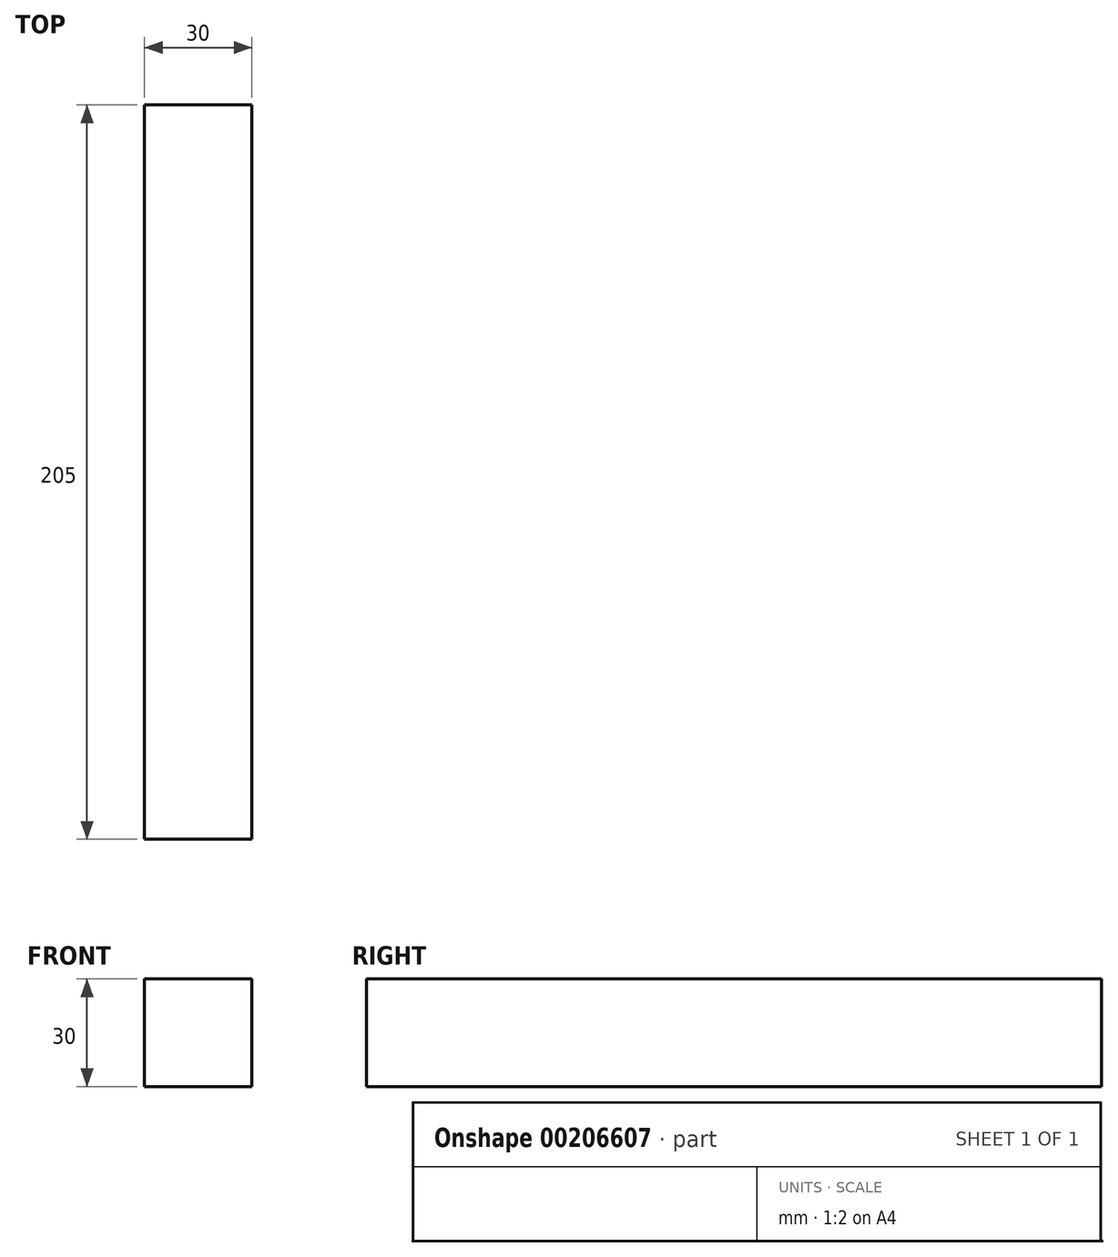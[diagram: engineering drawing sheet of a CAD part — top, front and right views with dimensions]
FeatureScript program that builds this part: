
annotation { "Feature Type Name" : "Feature", "Feature Type Description" : "" }
export const myFeature = defineFeature(function(context is Context, id is Id, definition is map)
    precondition{}
    {
        {
            var Q0;
            Q0=qCreatedBy(makeId("Front.planeOp"),FACE);
            var sketch = newSketch(context, id + "F0", { "sketchPlane" : qUnion([Q0])});
            skLineSegment(sketch, "E0.bottom", {"start": v(0, 0) * mm, "end": v(30, 0) * mm});
            skLineSegment(sketch, "E0.top", {"start": v(0, 30) * mm, "end": v(30, 30) * mm});
            skLineSegment(sketch, "E0.left", {"start": v(0, 0) * mm, "end": v(0, 30) * mm});
            skLineSegment(sketch, "E0.right", {"start": v(30, 0) * mm, "end": v(30, 30) * mm});
            skSolve(sketch);
        }
        {
            var Q0;
            Q0=makeQuery(id+"F0.imprint","IMPRINT",FACE,{"disambiguationData":[TD([[makeQuery(id+"F0.imprint","IMPRINT",EDGE,{"derivedFrom":sQuery(id+"F0.wireOp",EDGE,"E0.bottom")}),1.0]])]});
            extrude(context, id + "F1", {"entities" : qUnion([Q0]), "depth" : 205 * mm});
        }
    });
